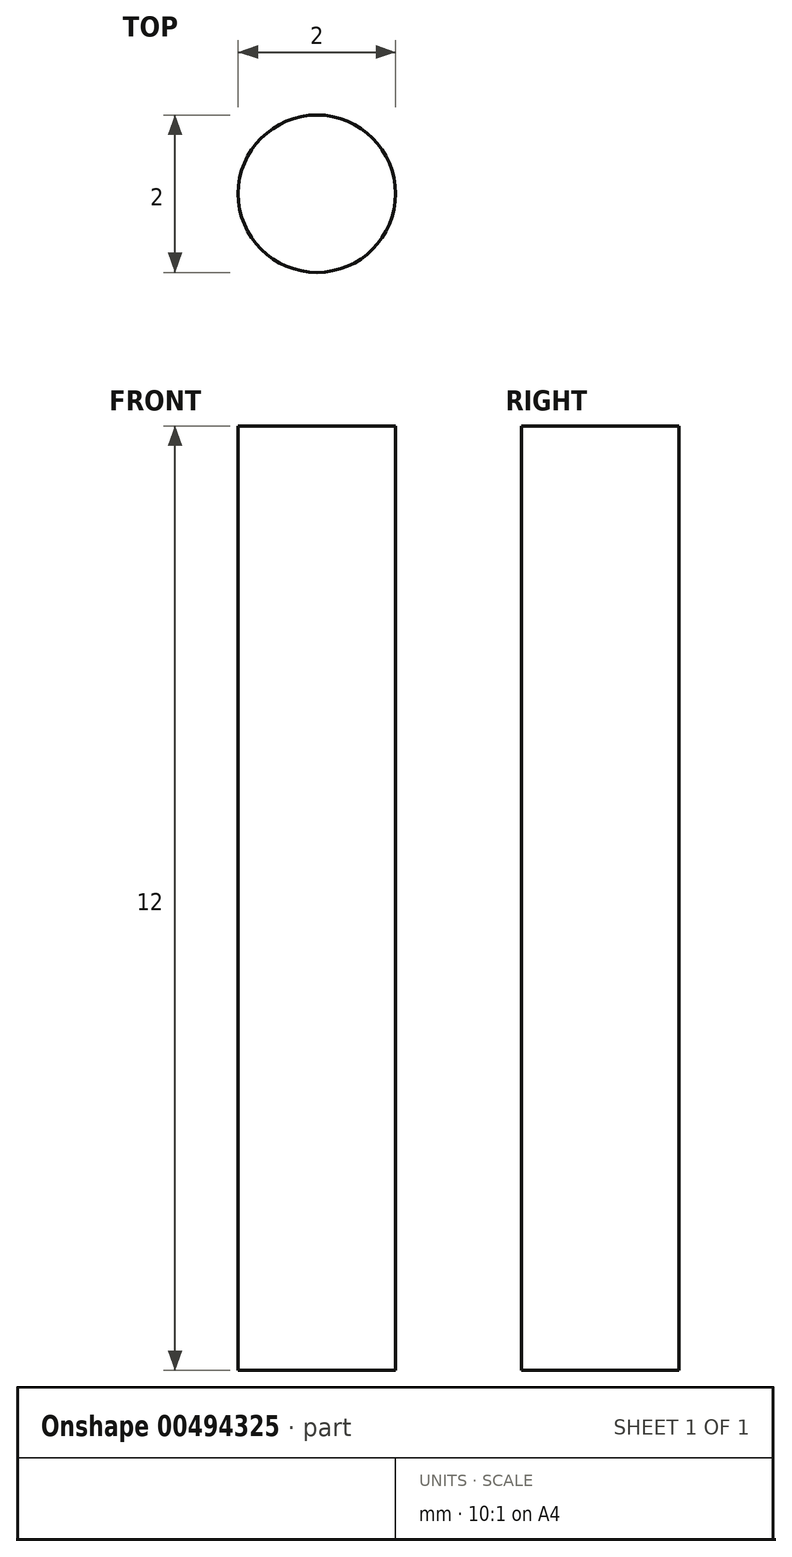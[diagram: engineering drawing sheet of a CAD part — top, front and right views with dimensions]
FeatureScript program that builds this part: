
annotation { "Feature Type Name" : "Feature", "Feature Type Description" : "" }
export const myFeature = defineFeature(function(context is Context, id is Id, definition is map)
    precondition{}
    {
        {
            var Q0;
            Q0=qCreatedBy(makeId("Top.planeOp"),FACE);
            var sketch = newSketch(context, id + "F0", { "sketchPlane" : qUnion([Q0])});
            skCircle(sketch, "E0", {"center": v(0, 0) * mm, "radius": 1 * mm});
            skSolve(sketch);
        }
        {
            var Q0;
            Q0=makeQuery(id+"F0.imprint","IMPRINT",FACE,{"disambiguationData":[TD([[makeQuery(id+"F0.imprint","IMPRINT",EDGE,{"derivedFrom":sQuery(id+"F0.wireOp",EDGE,"E0")}),1.0]])]});
            extrude(context, id + "F1", {"entities" : qUnion([Q0]), "depth" : 12 * mm});
        }
    });
